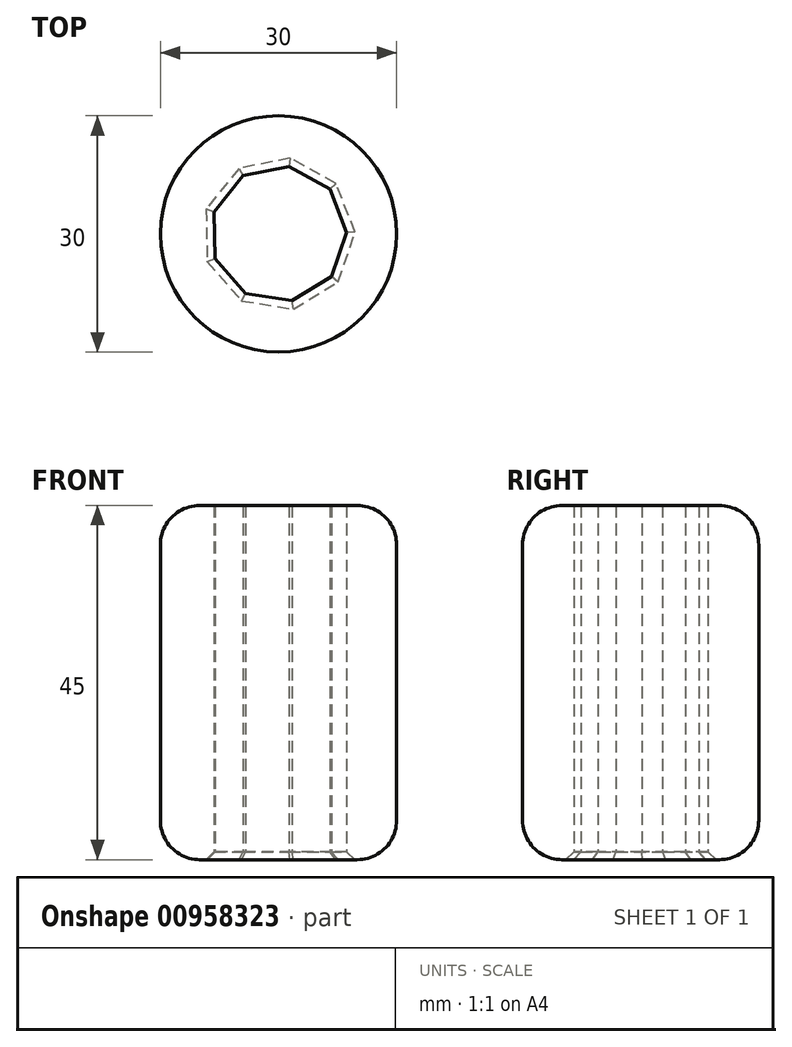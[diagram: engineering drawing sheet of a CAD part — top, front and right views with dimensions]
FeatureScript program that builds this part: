
annotation { "Feature Type Name" : "Feature", "Feature Type Description" : "" }
export const myFeature = defineFeature(function(context is Context, id is Id, definition is map)
    precondition{}
    {
        {
            var Q0;
            Q0=qCreatedBy(makeId("Top.planeOp"),FACE);
            var sketch = newSketch(context, id + "F0", { "sketchPlane" : qUnion([Q0])});
            skCircle(sketch, "E0", {"center": v(0, 0) * mm, "radius": 15 * mm});
            skCircle(sketch, "E1.cCircle", {"center": v(0, 0) * mm, "radius": 8.14 * mm, "construction": true});
            skLineSegment(sketch, "E1.0", {"start": v(1.32, 8.56) * mm, "end": v(6.51, 5.7) * mm});
            skLineSegment(sketch, "E1.1", {"start": v(6.51, 5.7) * mm, "end": v(8.66, 0.18) * mm});
            skLineSegment(sketch, "E1.2", {"start": v(8.66, 0.18) * mm, "end": v(6.75, -5.42) * mm});
            skLineSegment(sketch, "E1.3", {"start": v(6.75, -5.42) * mm, "end": v(1.68, -8.5) * mm});
            skLineSegment(sketch, "E1.4", {"start": v(1.68, -8.5) * mm, "end": v(-4.17, -7.59) * mm});
            skLineSegment(sketch, "E1.5", {"start": v(-4.17, -7.59) * mm, "end": v(-8.07, -3.13) * mm});
            skLineSegment(sketch, "E1.6", {"start": v(-8.07, -3.13) * mm, "end": v(-8.2, 2.79) * mm});
            skLineSegment(sketch, "E1.7", {"start": v(-8.2, 2.79) * mm, "end": v(-4.49, 7.4) * mm});
            skLineSegment(sketch, "E1.8", {"start": v(-4.49, 7.4) * mm, "end": v(1.32, 8.56) * mm});
            skPoint(sketch, "E1.0.midPoint", {"position": v(3.92, 7.13) * mm});
            skSolve(sketch);
        }
        {
            var Q0;
            Q0 = qSketchRegion(id + "F0", true);
            extrude(context, id + "F1", {"entities" : qUnion([Q0]), "depth" : 45 * mm, "offsetDistance" : 25 * mm});
        }
        {
            var Q0;
            Q0=makeQuery(id+"F1.opExtrude","CAP_EDGE",EDGE,{"disambiguationData":[OSD([sQuery(id+"F0.wireOp",EDGE,"E0")])],"isStart":false});
            var Q1;
            Q1=makeQuery(id+"F1.opExtrude","CAP_EDGE",EDGE,{"disambiguationData":[OSD([sQuery(id+"F0.wireOp",EDGE,"E0")])],"isStart":true});
            fillet(context, id + "F2", {"entities" : qUnion([Q0, Q1]), "radius" : 5 * mm, "tangentPropagation" : true, "allowEdgeOverflow" : false});
        }
        {
            var Q0;
            Q0=makeQuery(id+"F1.opExtrude","CAP_EDGE",EDGE,{"disambiguationData":[OSD([sQuery(id+"F0.wireOp",EDGE,"E1.3")])],"isStart":true});
            var Q1;
            Q1=makeQuery(id+"F1.opExtrude","CAP_EDGE",EDGE,{"disambiguationData":[OSD([sQuery(id+"F0.wireOp",EDGE,"E1.4")])],"isStart":true});
            var Q2;
            Q2=makeQuery(id+"F1.opExtrude","CAP_EDGE",EDGE,{"disambiguationData":[OSD([sQuery(id+"F0.wireOp",EDGE,"E1.5")])],"isStart":true});
            var Q3;
            Q3=makeQuery(id+"F1.opExtrude","CAP_EDGE",EDGE,{"disambiguationData":[OSD([sQuery(id+"F0.wireOp",EDGE,"E1.6")])],"isStart":true});
            var Q4;
            Q4=makeQuery(id+"F1.opExtrude","CAP_EDGE",EDGE,{"disambiguationData":[OSD([sQuery(id+"F0.wireOp",EDGE,"E1.7")])],"isStart":true});
            var Q5;
            Q5=makeQuery(id+"F1.opExtrude","CAP_EDGE",EDGE,{"disambiguationData":[OSD([sQuery(id+"F0.wireOp",EDGE,"E1.8")])],"isStart":true});
            var Q6;
            Q6=makeQuery(id+"F1.opExtrude","CAP_EDGE",EDGE,{"disambiguationData":[OSD([sQuery(id+"F0.wireOp",EDGE,"E1.0")])],"isStart":true});
            var Q7;
            Q7=makeQuery(id+"F1.opExtrude","CAP_EDGE",EDGE,{"disambiguationData":[OSD([sQuery(id+"F0.wireOp",EDGE,"E1.1")])],"isStart":true});
            var Q8;
            Q8=makeQuery(id+"F1.opExtrude","CAP_EDGE",EDGE,{"disambiguationData":[OSD([sQuery(id+"F0.wireOp",EDGE,"E1.2")])],"isStart":true});
            chamfer(context, id + "F3", {"entities" : qUnion([Q0, Q1, Q2, Q3, Q4, Q5, Q6, Q7, Q8]), "width" : 1 * mm, "tangentPropagation" : true});
        }
    });
